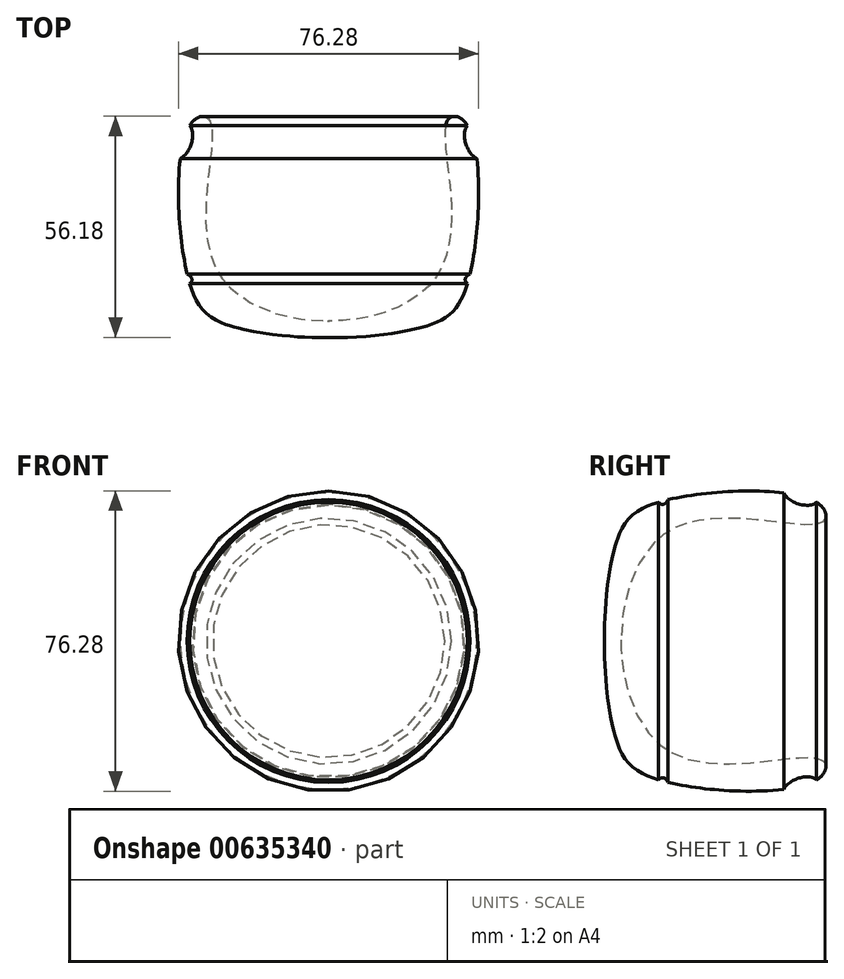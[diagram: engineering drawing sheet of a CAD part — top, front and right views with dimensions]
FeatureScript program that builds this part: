
annotation { "Feature Type Name" : "Feature", "Feature Type Description" : "" }
export const myFeature = defineFeature(function(context is Context, id is Id, definition is map)
    precondition{}
    {
        {
            var Q0;
            Q0=qCreatedBy(makeId("Top.planeOp"),FACE);
            var sketch = newSketch(context, id + "F0", { "sketchPlane" : qUnion([Q0])});
            skLineSegment(sketch, "E0", {"start": v(0, 75.28) * mm, "end": v(0, -74.97) * mm});
            skFitSpline(sketch, "E1", {"points": [v(-26.72, 18.78) * mm, v(-27.64, -26.42) * mm, v(21.83, -34.66) * mm, v(35.27, -23.06) * mm, v(34.97, 17.56) * mm, v(30.08, 18.17) * mm, v(27.03, -21.83) * mm, v(-23.06, -22.75) * mm, v(-19.4, 21.83) * mm, v(-23.36, 22.75) * mm, v(-26.72, 18.78) * mm]});
            skFitSpline(sketch, "E2", {"points": [v(37.65, 8.73) * mm, v(50.24, 8.7) * mm, v(57.56, -14.2) * mm, v(35.92, -20.63) * mm, v(35.27, -23.06) * mm, v(61.23, -18.17) * mm, v(57.56, 8.1) * mm, v(35.27, 17.1) * mm, v(37.65, 8.73) * mm]});
            skSolve(sketch);
        }
        {
            var Q0;
            {var subQ1=sQuery(id+"F0.wireOp",EDGE,"E1");var subQ4=sQuery(id+"F0.wireOp",EDGE,"E0");var subQ5=makeQuery(id+"F0.imprint","INTERSECT",VERTEX,{"disambiguationData":[OD(0.0)],"derivedFrom":[subQ4,subQ1]});Q0=makeQuery(id+"F0.imprint","IMPRINT",FACE,{"disambiguationData":[TD([[makeQuery(id+"F0.imprint","IMPRINT",EDGE,{"disambiguationData":[TD([[subQ5,1.0]])],"derivedFrom":subQ4}),1.0]])]});}
            var Q1;
            Q1=sQuery(id+"F0.wireOp",EDGE,"E0");
            revolve(context, id + "F1", {"entities" : qUnion([Q0]), "axis" : qUnion([Q1]), "revolveType" : RevolveType.FULL});
        }
    });
